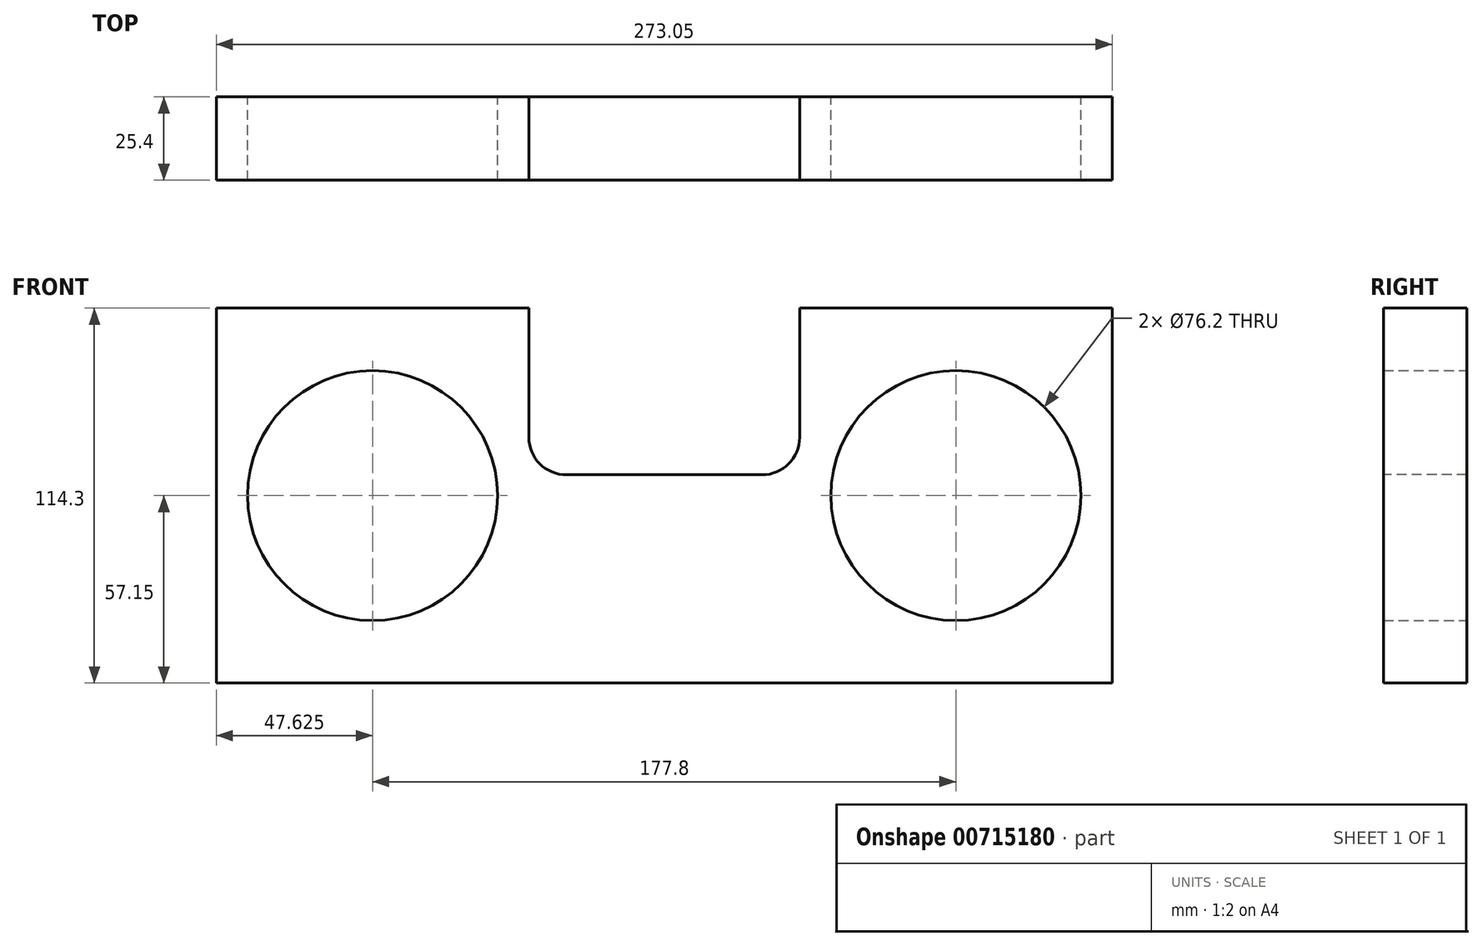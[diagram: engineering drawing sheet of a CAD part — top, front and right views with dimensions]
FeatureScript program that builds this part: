
annotation { "Feature Type Name" : "Feature", "Feature Type Description" : "" }
export const myFeature = defineFeature(function(context is Context, id is Id, definition is map)
    precondition{}
    {
        {
            var Q0;
            Q0=qCreatedBy(makeId("Front.planeOp"),FACE);
            var sketch = newSketch(context, id + "F0", { "sketchPlane" : qUnion([Q0])});
            skLineSegment(sketch, "E0.bottom", {"start": v(0, 0) * mm, "end": v(273.05, 0) * mm});
            skLineSegment(sketch, "E0.top", {"start": v(0, 114.3) * mm, "end": v(273.05, 114.3) * mm});
            skLineSegment(sketch, "E0.left", {"start": v(0, 0) * mm, "end": v(0, 114.3) * mm});
            skLineSegment(sketch, "E0.right", {"start": v(273.05, 0) * mm, "end": v(273.05, 114.3) * mm});
            skCircle(sketch, "E1", {"center": v(47.62, 57.15) * mm, "radius": 38.1 * mm});
            skCircle(sketch, "E2", {"center": v(225.43, 57.15) * mm, "radius": 38.1 * mm});
            skSolve(sketch);
        }
        {
            var Q0;
            Q0=qSketchRegion(id+"F0",true);
            extrude(context, id + "F1", {"entities" : qUnion([Q0]), "depth" : 25.4 * mm, "offsetDistance" : 25.4 * mm});
        }
        {
            var Q0;
            Q0=makeQuery(id+"F1.opExtrude","CAP_FACE",FACE,{"disambiguationData":[OSD([sQuery(id+"F0.wireOp",EDGE,"E0.bottom"),sQuery(id+"F0.wireOp",EDGE,"E0.top"),sQuery(id+"F0.wireOp",EDGE,"E0.left"),sQuery(id+"F0.wireOp",EDGE,"E0.right"),sQuery(id+"F0.wireOp",EDGE,"E1"),sQuery(id+"F0.wireOp",EDGE,"E2")])],"isStart":false});
            var sketch = newSketch(context, id + "F2", { "sketchPlane" : qUnion([Q0])});
            skLineSegment(sketch, "E3", {"start": v(95.25, 114.3) * mm, "end": v(95.25, 74.93) * mm});
            skLineSegment(sketch, "E4", {"start": v(106.68, 63.5) * mm, "end": v(166.37, 63.5) * mm});
            skLineSegment(sketch, "E5", {"start": v(177.8, 74.93) * mm, "end": v(177.8, 114.3) * mm});
            skPoint(sketch, "E6.visualSharp", {"position": v(95.25, 63.5) * mm});
            skArc(sketch, "E6.filletArc", {"start": v(95.25, 74.93) * mm, "mid": v(98.6, 66.85) * mm, "end": v(106.68, 63.5) * mm});
            skPoint(sketch, "E7.visualSharp", {"position": v(177.8, 63.5) * mm});
            skArc(sketch, "E7.filletArc", {"start": v(166.37, 63.5) * mm, "mid": v(174.45, 66.85) * mm, "end": v(177.8, 74.93) * mm});
            skSolve(sketch);
        }
        {
            var Q0;
            Q0=qSketchRegion(id+"F2",true);
            var Q1;
            {var subQ1=sQuery(id+"F2.wireOp",EDGE,"E3");Q1=makeQuery(id+"F2.imprint","IMPRINT",FACE,{"disambiguationData":[TD([[makeQuery(id+"F2.imprint","IMPRINT",EDGE,{"derivedFrom":subQ1}),1.0]])]});}
            extrude(context, id + "F3", {"entities" : qUnion([Q0, Q1]), "operationType" : NewBodyOperationType.REMOVE, "oppositeDirection" : true, "depth" : 25.4 * mm, "offsetDistance" : 25.4 * mm});
        }
    });
